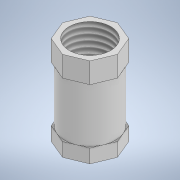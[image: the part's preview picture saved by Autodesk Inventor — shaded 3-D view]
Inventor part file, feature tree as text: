
AUTODESK INVENTOR PART (.ipt)
format: ipt  version: 2022 (Build 260153000, 153)  size: 158,720 bytes
history: native  units: mm
features: sketch x4, extrude x3, other x1, hole x1
ambient origin geometry x8: Origin, YZ Plane, XZ Plane, XY Plane, X Axis, Y Axis, Z Axis, Center Point
bodies: Body1 (feature_tree)
feature tree (9):
  other  "Sólido1"
  extrude  "Extrusión1"  Depth=5.0mm TaperAngle=0.0deg
  extrude  "Extrusión2"  Depth=20.0mm
  extrude  "Extrusión3"  [1 undecoded]
  hole  "Agujero1"  [1 undecoded]
  sketch  "Boceto1"  dims[d0=20.0mm d1=5.0mm d2=0.0mm]
  sketch  "Boceto2"  dims[d3=20.0mm d4=0.0mm d5=20.0mm]
  sketch  "Boceto3"  dims[d6=7.5mm d7=0.0mm]
  sketch  "Boceto4"  dims[d8=15.1638mm d9=32.5mm d10=4.0mm d11=2.0mm d12=90.0deg d13=8.0mm d14=20.594885mm]
note: 2 required parameter values undecoded (feature->parameter linkage not recoverable at this tier; creation-order binding heuristic only, values carry confidence <= 0.55)
